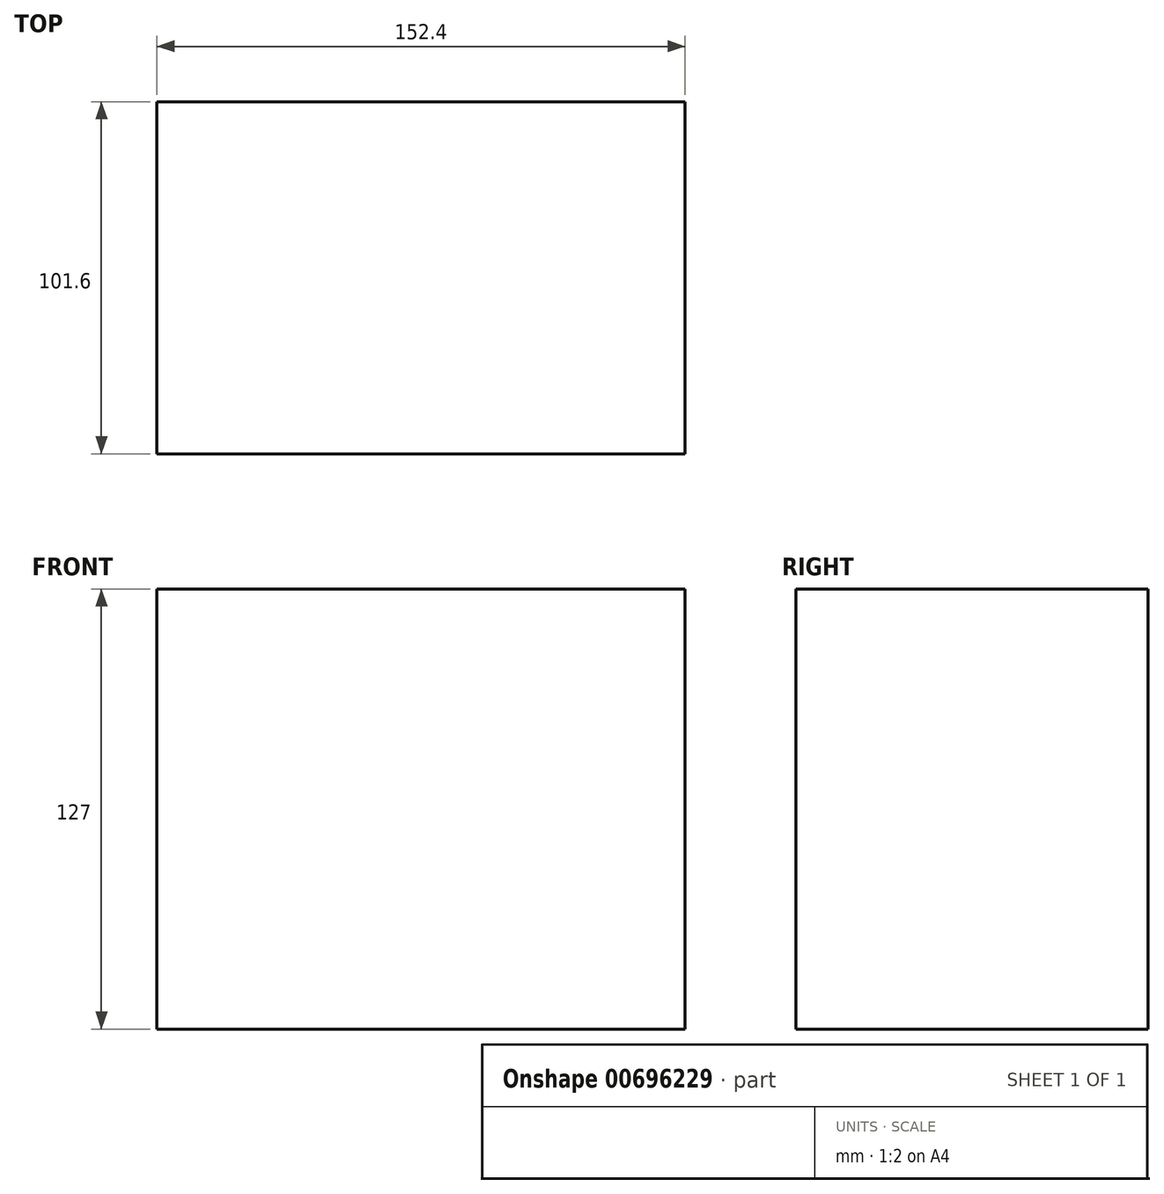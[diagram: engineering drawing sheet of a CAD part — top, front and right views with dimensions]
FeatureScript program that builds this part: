
annotation { "Feature Type Name" : "Feature", "Feature Type Description" : "" }
export const myFeature = defineFeature(function(context is Context, id is Id, definition is map)
    precondition{}
    {
        {
            var Q0;
            Q0=qCreatedBy(makeId("Front.planeOp"),FACE);
            var sketch = newSketch(context, id + "F0", { "sketchPlane" : qUnion([Q0])});
            skLineSegment(sketch, "E0", {"start": v(0, 0) * mm, "end": v(152.4, 0) * mm});
            skLineSegment(sketch, "E1", {"start": v(0, 0) * mm, "end": v(0, 127) * mm});
            skLineSegment(sketch, "E2", {"start": v(0, 127) * mm, "end": v(152.4, 127) * mm});
            skLineSegment(sketch, "E3", {"start": v(152.4, 0) * mm, "end": v(152.4, 127) * mm});
            skSolve(sketch);
        }
        {
            var Q0;
            Q0=makeQuery(id+"F0.imprint","IMPRINT",FACE,{"disambiguationData":[TD([[makeQuery(id+"F0.imprint","IMPRINT",EDGE,{"derivedFrom":sQuery(id+"F0.wireOp",EDGE,"E0")}),1.0]])]});
            extrude(context, id + "F1", {"entities" : qUnion([Q0]), "oppositeDirection" : true, "depth" : 101.6 * mm, "offsetDistance" : 25.4 * mm});
        }
    });
